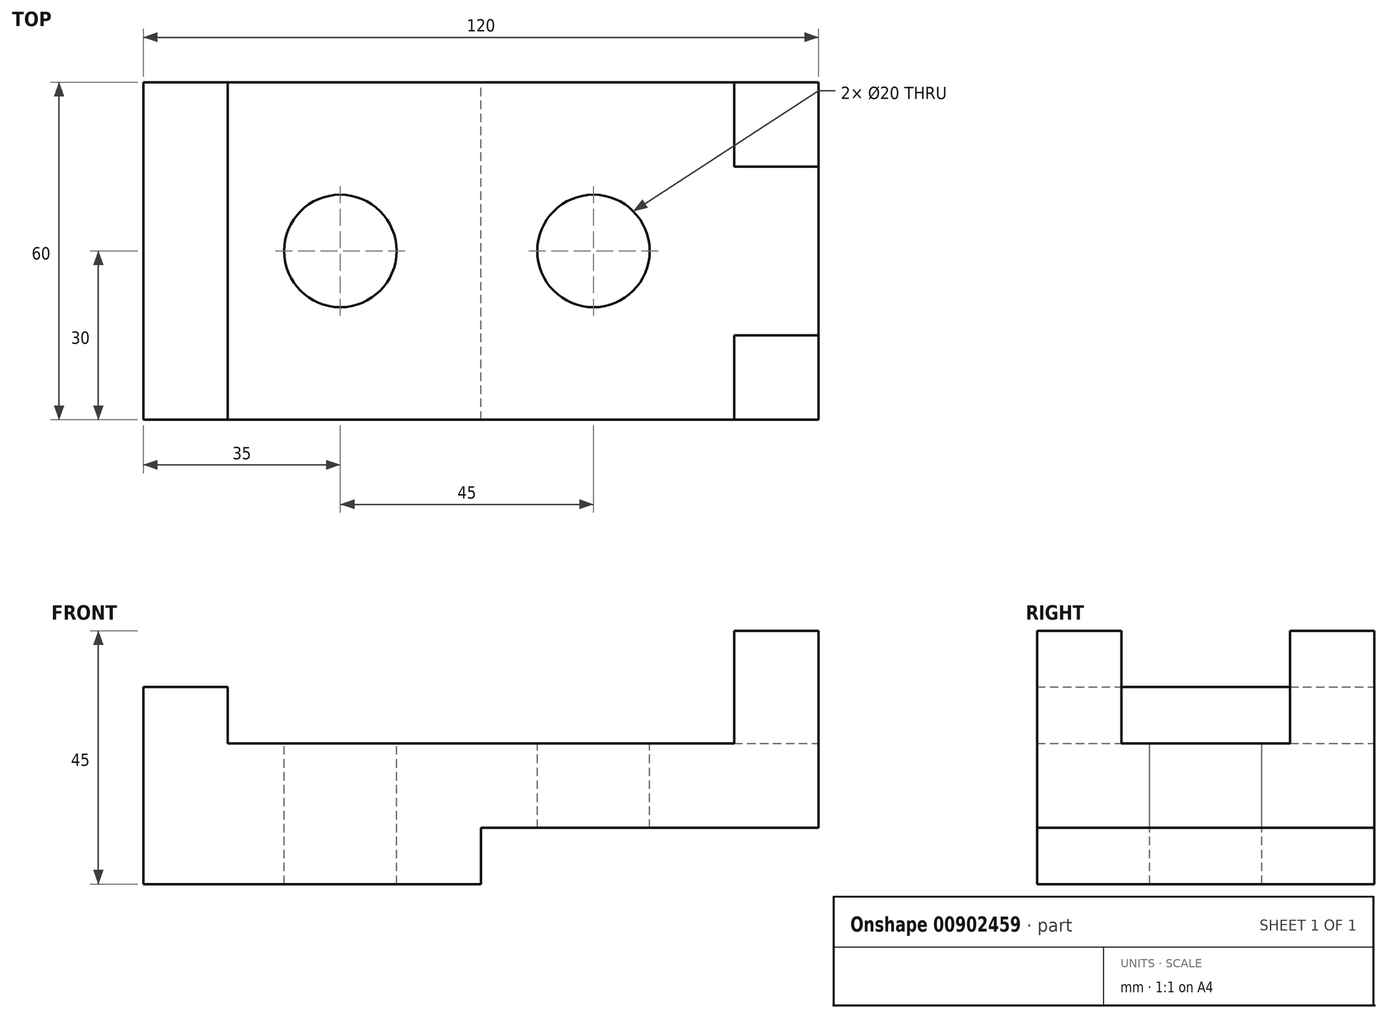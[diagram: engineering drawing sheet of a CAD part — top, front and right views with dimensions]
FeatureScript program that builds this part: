
annotation { "Feature Type Name" : "Feature", "Feature Type Description" : "" }
export const myFeature = defineFeature(function(context is Context, id is Id, definition is map)
    precondition{}
    {
        {
            var Q0;
            Q0=qCreatedBy(makeId("Front.planeOp"),FACE);
            var sketch = newSketch(context, id + "F0", { "sketchPlane" : qUnion([Q0])});
            skLineSegment(sketch, "E0", {"start": v(0, 0) * mm, "end": v(60, 0) * mm});
            skLineSegment(sketch, "E1", {"start": v(60, 0) * mm, "end": v(60, 10) * mm});
            skLineSegment(sketch, "E2", {"start": v(60, 10) * mm, "end": v(120, 10) * mm});
            skLineSegment(sketch, "E3", {"start": v(120, 10) * mm, "end": v(120, 45) * mm});
            skLineSegment(sketch, "E4", {"start": v(120, 45) * mm, "end": v(105, 45) * mm});
            skLineSegment(sketch, "E5", {"start": v(105, 45) * mm, "end": v(105, 25) * mm});
            skLineSegment(sketch, "E6", {"start": v(105, 25) * mm, "end": v(15, 25) * mm});
            skLineSegment(sketch, "E7", {"start": v(15, 25) * mm, "end": v(15, 35) * mm});
            skLineSegment(sketch, "E8", {"start": v(15, 35) * mm, "end": v(0, 35) * mm});
            skLineSegment(sketch, "E9", {"start": v(0, 35) * mm, "end": v(0, 0) * mm});
            skSolve(sketch);
        }
        {
            var Q0;
            Q0=makeQuery(id+"F0.imprint","IMPRINT",FACE,{"disambiguationData":[TD([[makeQuery(id+"F0.imprint","IMPRINT",EDGE,{"derivedFrom":sQuery(id+"F0.wireOp",EDGE,"E0")}),1.0]])]});
            extrude(context, id + "F1", {"entities" : qUnion([Q0]), "endBound" : BoundingType.SYMMETRIC, "depth" : 60 * mm, "offsetDistance" : 25 * mm});
        }
        {
            var Q0;
            Q0=makeQuery(id+"F1.opExtrude","SWEPT_FACE",FACE,{"disambiguationData":[OSD([sQuery(id+"F0.wireOp",EDGE,"E3")])]});
            var sketch = newSketch(context, id + "F2", { "sketchPlane" : qUnion([Q0])});
            skLineSegment(sketch, "E10.bottom", {"start": v(-15, 50) * mm, "end": v(15, 50) * mm});
            skLineSegment(sketch, "E10.top", {"start": v(-15, 25) * mm, "end": v(15, 25) * mm});
            skLineSegment(sketch, "E10.left", {"start": v(-15, 50) * mm, "end": v(-15, 25) * mm});
            skLineSegment(sketch, "E10.right", {"start": v(15, 50) * mm, "end": v(15, 25) * mm});
            skSolve(sketch);
        }
        {
            var Q0;
            {var subQ0=sQuery(id+"F2.wireOp",EDGE,"E10.top");Q0=makeQuery(id+"F2.imprint","IMPRINT",FACE,{"disambiguationData":[TD([[makeQuery(id+"F2.imprint","IMPRINT",EDGE,{"derivedFrom":subQ0}),1.0]])]});}
            extrude(context, id + "F3", {"entities" : qUnion([Q0]), "operationType" : NewBodyOperationType.REMOVE, "oppositeDirection" : true, "depth" : 25 * mm, "offsetDistance" : 25 * mm});
        }
        {
            var Q0;
            Q0=makeQuery(id+"F3.boolean.opBoolean","MERGE",FACE,{"derivedFrom":[makeQuery(id+"F1.opExtrude","SWEPT_FACE",FACE,{"disambiguationData":[OSD([sQuery(id+"F0.wireOp",EDGE,"E6")])]})],"fromTools":[makeQuery(id+"F3.opExtrude","SWEPT_FACE",FACE,{"disambiguationData":[OSD([sQuery(id+"F2.wireOp",EDGE,"E10.top")])]})]});
            var sketch = newSketch(context, id + "F4", { "sketchPlane" : qUnion([Q0])});
            skPoint(sketch, "E11", {"position": v(35, 0) * mm});
            skPoint(sketch, "E12", {"position": v(80, 0) * mm});
            skSolve(sketch);
        }
        {
            var Q0;
            Q0=sQuery(id+"F4.wireOp",VERTEX,"E11");
            var Q1;
            Q1=sQuery(id+"F4.wireOp",VERTEX,"E12");
            var Q2;
            Q2=makeQuery(id+"F1.opExtrude","SWEPT_BODY",BODY,{"disambiguationData":[OSD([sQuery(id+"F0.wireOp",EDGE,"E0"),sQuery(id+"F0.wireOp",EDGE,"E1"),sQuery(id+"F0.wireOp",EDGE,"E2"),sQuery(id+"F0.wireOp",EDGE,"E3"),sQuery(id+"F0.wireOp",EDGE,"E4"),sQuery(id+"F0.wireOp",EDGE,"E5"),sQuery(id+"F0.wireOp",EDGE,"E6"),sQuery(id+"F0.wireOp",EDGE,"E7"),sQuery(id+"F0.wireOp",EDGE,"E8"),sQuery(id+"F0.wireOp",EDGE,"E9")])]});
            hole(context, id + "F5", {"style" : HoleStyle.SIMPLE, "endStyle" : HoleEndStyle.THROUGH, "holeDiameter" : 20 * mm, "majorDiameter" : 5 * mm, "isTappedThrough" : true, "tappedDepth" : 12 * mm, "tapClearance" : 3, "locations" : qUnion([Q0, Q1]), "scope" : qUnion([Q2])});
        }
    });
